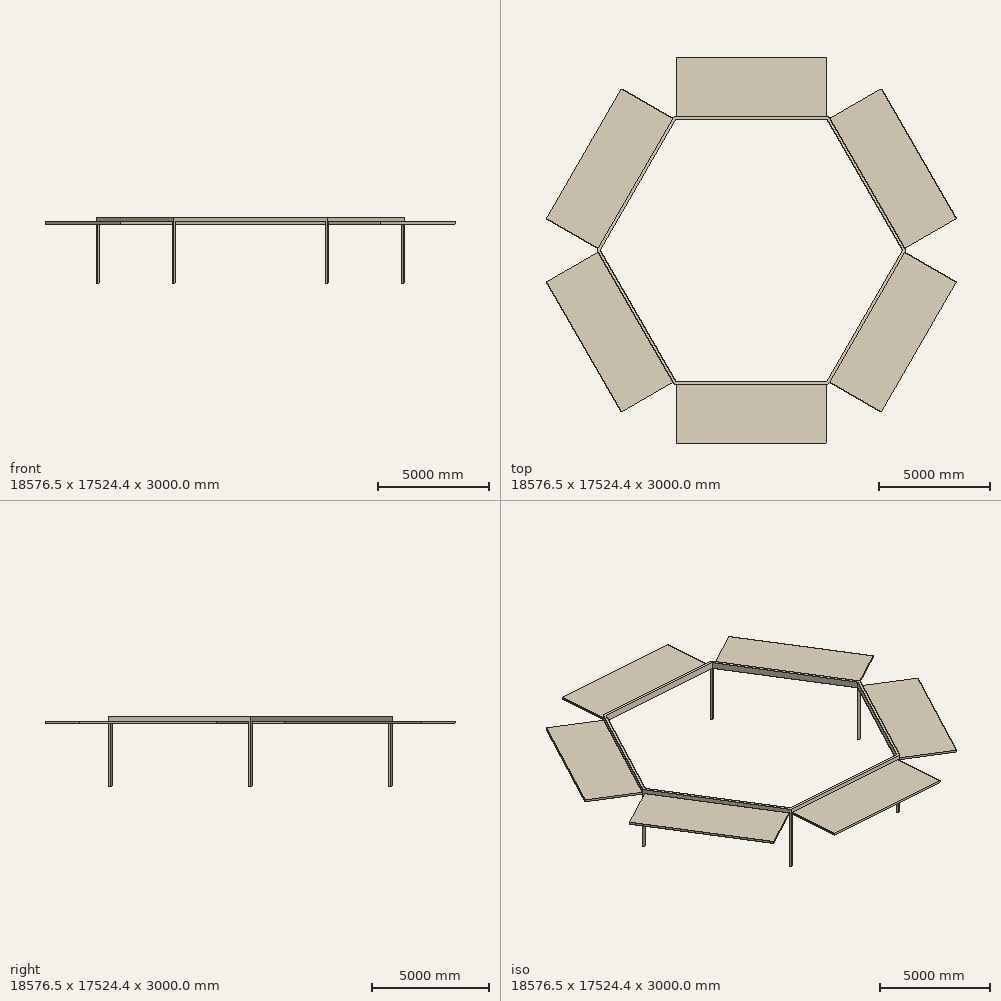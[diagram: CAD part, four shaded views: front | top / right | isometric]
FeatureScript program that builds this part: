
annotation { "Feature Type Name" : "Feature", "Feature Type Description" : "" }
export const myFeature = defineFeature(function(context is Context, id is Id, definition is map)
    precondition{}
    {
        {
            var Q0;
            Q0=qCreatedBy(makeId("Top.planeOp"),FACE);
            var sketch = newSketch(context, id + "F0", { "sketchPlane" : qUnion([Q0])});
            skCircle(sketch, "E0.cCircle", {"center": v(0, 0) * mm, "radius": 7000 * mm, "construction": true});
            skLineSegment(sketch, "E0.0", {"start": v(7000, 0) * mm, "end": v(3500, -6062.18) * mm});
            skLineSegment(sketch, "E0.1", {"start": v(3500, -6062.18) * mm, "end": v(-3500, -6062.18) * mm});
            skLineSegment(sketch, "E0.2", {"start": v(-3500, -6062.18) * mm, "end": v(-7000, 0) * mm});
            skLineSegment(sketch, "E0.3", {"start": v(-7000, 0) * mm, "end": v(-3500, 6062.18) * mm});
            skLineSegment(sketch, "E0.4", {"start": v(-3500, 6062.18) * mm, "end": v(3500, 6062.18) * mm});
            skLineSegment(sketch, "E0.5", {"start": v(3500, 6062.18) * mm, "end": v(7000, 0) * mm});
            skCircle(sketch, "E1.cCircle", {"center": v(0, 0) * mm, "radius": 6850 * mm, "construction": true});
            skLineSegment(sketch, "E1.0", {"start": v(6850, 0) * mm, "end": v(3425, -5932.27) * mm});
            skLineSegment(sketch, "E1.1", {"start": v(3425, -5932.27) * mm, "end": v(-3425, -5932.27) * mm});
            skLineSegment(sketch, "E1.2", {"start": v(-3425, -5932.27) * mm, "end": v(-6850, 0) * mm});
            skLineSegment(sketch, "E1.3", {"start": v(-6850, 0) * mm, "end": v(-3425, 5932.27) * mm});
            skLineSegment(sketch, "E1.4", {"start": v(-3425, 5932.27) * mm, "end": v(3425, 5932.27) * mm});
            skLineSegment(sketch, "E1.5", {"start": v(3425, 5932.27) * mm, "end": v(6850, 0) * mm});
            skSolve(sketch);
        }
        {
            var Q0;
            Q0 = qSketchRegion(id + "F0", true);
            extrude(context, id + "F1", {"entities" : qUnion([Q0]), "depth" : 3000 * mm, "offsetDistance" : 25 * mm});
        }
        {
            var Q0;
            Q0=makeQuery(id+"F1.opExtrude","SWEPT_FACE",FACE,{"disambiguationData":[OSD([sQuery(id+"F0.wireOp",EDGE,"E0.2")])]});
            var sketch = newSketch(context, id + "F2", { "sketchPlane" : qUnion([Q0])});
            skLineSegment(sketch, "E2.bottom", {"start": v(-3400, 2700) * mm, "end": v(3400, 2700) * mm});
            skLineSegment(sketch, "E2.top", {"start": v(-3400, 0) * mm, "end": v(3400, 0) * mm});
            skLineSegment(sketch, "E2.left", {"start": v(-3400, 2700) * mm, "end": v(-3400, 0) * mm});
            skLineSegment(sketch, "E2.right", {"start": v(3400, 2700) * mm, "end": v(3400, 0) * mm});
            skSolve(sketch);
        }
        {
            var Q0;
            Q0 = qSketchRegion(id + "F2", true);
            extrude(context, id + "F3", {"entities" : qUnion([Q0]), "operationType" : NewBodyOperationType.REMOVE, "endBound" : BoundingType.THROUGH_ALL, "oppositeDirection" : true, "depth" : 7000 * mm, "offsetDistance" : 25 * mm});
        }
        {
            var Q0;
            Q0=makeQuery(id+"F1.opExtrude","SWEPT_FACE",FACE,{"disambiguationData":[OSD([sQuery(id+"F0.wireOp",EDGE,"E0.3")])]});
            var sketch = newSketch(context, id + "F4", { "sketchPlane" : qUnion([Q0])});
            skLineSegment(sketch, "E3.bottom", {"start": v(-3400, 2700) * mm, "end": v(3400, 2700) * mm});
            skLineSegment(sketch, "E3.top", {"start": v(-3400, 0) * mm, "end": v(3400, 0) * mm});
            skLineSegment(sketch, "E3.left", {"start": v(-3400, 2700) * mm, "end": v(-3400, 0) * mm});
            skLineSegment(sketch, "E3.right", {"start": v(3400, 2700) * mm, "end": v(3400, 0) * mm});
            skSolve(sketch);
        }
        {
            var Q0;
            Q0 = qSketchRegion(id + "F4", true);
            extrude(context, id + "F5", {"entities" : qUnion([Q0]), "operationType" : NewBodyOperationType.REMOVE, "endBound" : BoundingType.THROUGH_ALL, "oppositeDirection" : true, "depth" : 25 * mm, "offsetDistance" : 25 * mm});
        }
        {
            var Q0;
            Q0=makeQuery(id+"F1.opExtrude","SWEPT_FACE",FACE,{"disambiguationData":[OSD([sQuery(id+"F0.wireOp",EDGE,"E0.4")])]});
            var sketch = newSketch(context, id + "F6", { "sketchPlane" : qUnion([Q0])});
            skLineSegment(sketch, "E4.bottom", {"start": v(-3400, 0) * mm, "end": v(3400, 0) * mm});
            skLineSegment(sketch, "E4.top", {"start": v(-3400, 2700) * mm, "end": v(3400, 2700) * mm});
            skLineSegment(sketch, "E4.left", {"start": v(-3400, 0) * mm, "end": v(-3400, 2700) * mm});
            skLineSegment(sketch, "E4.right", {"start": v(3400, 0) * mm, "end": v(3400, 2700) * mm});
            skSolve(sketch);
        }
        {
            var Q0;
            Q0 = qSketchRegion(id + "F6", true);
            extrude(context, id + "F7", {"entities" : qUnion([Q0]), "operationType" : NewBodyOperationType.REMOVE, "endBound" : BoundingType.THROUGH_ALL, "oppositeDirection" : true, "depth" : 25 * mm, "offsetDistance" : 25 * mm});
        }
        {
            var Q0;
            Q0=makeQuery(id+"F1.opExtrude","SWEPT_FACE",FACE,{"disambiguationData":[OSD([sQuery(id+"F0.wireOp",EDGE,"E0.4")])]});
            var sketch = newSketch(context, id + "F8", { "sketchPlane" : qUnion([Q0])});
            skLineSegment(sketch, "E5.bottom", {"start": v(-3400, 2700) * mm, "end": v(3400, 2700) * mm});
            skLineSegment(sketch, "E5.top", {"start": v(-3400, 2800) * mm, "end": v(3400, 2800) * mm});
            skLineSegment(sketch, "E5.left", {"start": v(-3400, 2700) * mm, "end": v(-3400, 2800) * mm});
            skLineSegment(sketch, "E5.right", {"start": v(3400, 2700) * mm, "end": v(3400, 2800) * mm});
            skSolve(sketch);
        }
        {
            var Q0;
            Q0 = qSketchRegion(id + "F8", true);
            extrude(context, id + "F9", {"entities" : qUnion([Q0]), "operationType" : NewBodyOperationType.ADD, "depth" : 2700 * mm, "offsetDistance" : 25 * mm});
        }
        {
            var Q0;
            Q0=makeQuery(id+"F1.opExtrude","SWEPT_FACE",FACE,{"disambiguationData":[OSD([sQuery(id+"F0.wireOp",EDGE,"E0.5")])]});
            var sketch = newSketch(context, id + "F10", { "sketchPlane" : qUnion([Q0])});
            skLineSegment(sketch, "E6.bottom", {"start": v(-3400, 2700) * mm, "end": v(3400, 2700) * mm});
            skLineSegment(sketch, "E6.top", {"start": v(-3400, 2800) * mm, "end": v(3400, 2800) * mm});
            skLineSegment(sketch, "E6.left", {"start": v(-3400, 2700) * mm, "end": v(-3400, 2800) * mm});
            skLineSegment(sketch, "E6.right", {"start": v(3400, 2700) * mm, "end": v(3400, 2800) * mm});
            skSolve(sketch);
        }
        {
            var Q0;
            Q0 = qSketchRegion(id + "F10", true);
            extrude(context, id + "F11", {"entities" : qUnion([Q0]), "operationType" : NewBodyOperationType.ADD, "depth" : 2700 * mm, "offsetDistance" : 25 * mm});
        }
        {
            var Q0;
            Q0=makeQuery(id+"F1.opExtrude","SWEPT_FACE",FACE,{"disambiguationData":[OSD([sQuery(id+"F0.wireOp",EDGE,"E0.0")])]});
            var sketch = newSketch(context, id + "F12", { "sketchPlane" : qUnion([Q0])});
            skLineSegment(sketch, "E7.bottom", {"start": v(-3400, 2700) * mm, "end": v(3400, 2700) * mm});
            skLineSegment(sketch, "E7.top", {"start": v(-3400, 2800) * mm, "end": v(3400, 2800) * mm});
            skLineSegment(sketch, "E7.left", {"start": v(-3400, 2700) * mm, "end": v(-3400, 2800) * mm});
            skLineSegment(sketch, "E7.right", {"start": v(3400, 2700) * mm, "end": v(3400, 2800) * mm});
            skSolve(sketch);
        }
        {
            var Q0;
            Q0 = qSketchRegion(id + "F12", true);
            extrude(context, id + "F13", {"entities" : qUnion([Q0]), "operationType" : NewBodyOperationType.ADD, "depth" : 2700 * mm, "offsetDistance" : 25 * mm});
        }
        {
            var Q0;
            Q0=makeQuery(id+"F1.opExtrude","SWEPT_FACE",FACE,{"disambiguationData":[OSD([sQuery(id+"F0.wireOp",EDGE,"E0.1")])]});
            var sketch = newSketch(context, id + "F14", { "sketchPlane" : qUnion([Q0])});
            skLineSegment(sketch, "E8.bottom", {"start": v(-3400, 2700) * mm, "end": v(3400, 2700) * mm});
            skLineSegment(sketch, "E8.top", {"start": v(-3400, 2800) * mm, "end": v(3400, 2800) * mm});
            skLineSegment(sketch, "E8.left", {"start": v(-3400, 2700) * mm, "end": v(-3400, 2800) * mm});
            skLineSegment(sketch, "E8.right", {"start": v(3400, 2700) * mm, "end": v(3400, 2800) * mm});
            skSolve(sketch);
        }
        {
            var Q0;
            Q0 = qSketchRegion(id + "F14", true);
            extrude(context, id + "F15", {"entities" : qUnion([Q0]), "operationType" : NewBodyOperationType.ADD, "depth" : 2700 * mm, "offsetDistance" : 25 * mm});
        }
        {
            var Q0;
            Q0=makeQuery(id+"F1.opExtrude","SWEPT_FACE",FACE,{"disambiguationData":[OSD([sQuery(id+"F0.wireOp",EDGE,"E0.2")])]});
            var sketch = newSketch(context, id + "F16", { "sketchPlane" : qUnion([Q0])});
            skLineSegment(sketch, "E9.bottom", {"start": v(-3400, 2700) * mm, "end": v(3400, 2700) * mm});
            skLineSegment(sketch, "E9.top", {"start": v(-3400, 2800) * mm, "end": v(3400, 2800) * mm});
            skLineSegment(sketch, "E9.left", {"start": v(-3400, 2700) * mm, "end": v(-3400, 2800) * mm});
            skLineSegment(sketch, "E9.right", {"start": v(3400, 2700) * mm, "end": v(3400, 2800) * mm});
            skSolve(sketch);
        }
        {
            var Q0;
            Q0 = qSketchRegion(id + "F16", true);
            extrude(context, id + "F17", {"entities" : qUnion([Q0]), "operationType" : NewBodyOperationType.ADD, "depth" : 2700 * mm, "offsetDistance" : 25 * mm});
        }
        {
            var Q0;
            Q0=makeQuery(id+"F1.opExtrude","SWEPT_FACE",FACE,{"disambiguationData":[OSD([sQuery(id+"F0.wireOp",EDGE,"E0.3")])]});
            var sketch = newSketch(context, id + "F18", { "sketchPlane" : qUnion([Q0])});
            skLineSegment(sketch, "E10.bottom", {"start": v(-3400, 2700) * mm, "end": v(3400, 2700) * mm});
            skLineSegment(sketch, "E10.top", {"start": v(-3400, 2800) * mm, "end": v(3400, 2800) * mm});
            skLineSegment(sketch, "E10.left", {"start": v(-3400, 2700) * mm, "end": v(-3400, 2800) * mm});
            skLineSegment(sketch, "E10.right", {"start": v(3400, 2700) * mm, "end": v(3400, 2800) * mm});
            skSolve(sketch);
        }
        {
            var Q0;
            Q0 = qSketchRegion(id + "F18", true);
            extrude(context, id + "F19", {"entities" : qUnion([Q0]), "operationType" : NewBodyOperationType.ADD, "depth" : 2700 * mm, "offsetDistance" : 25 * mm});
        }
    });
